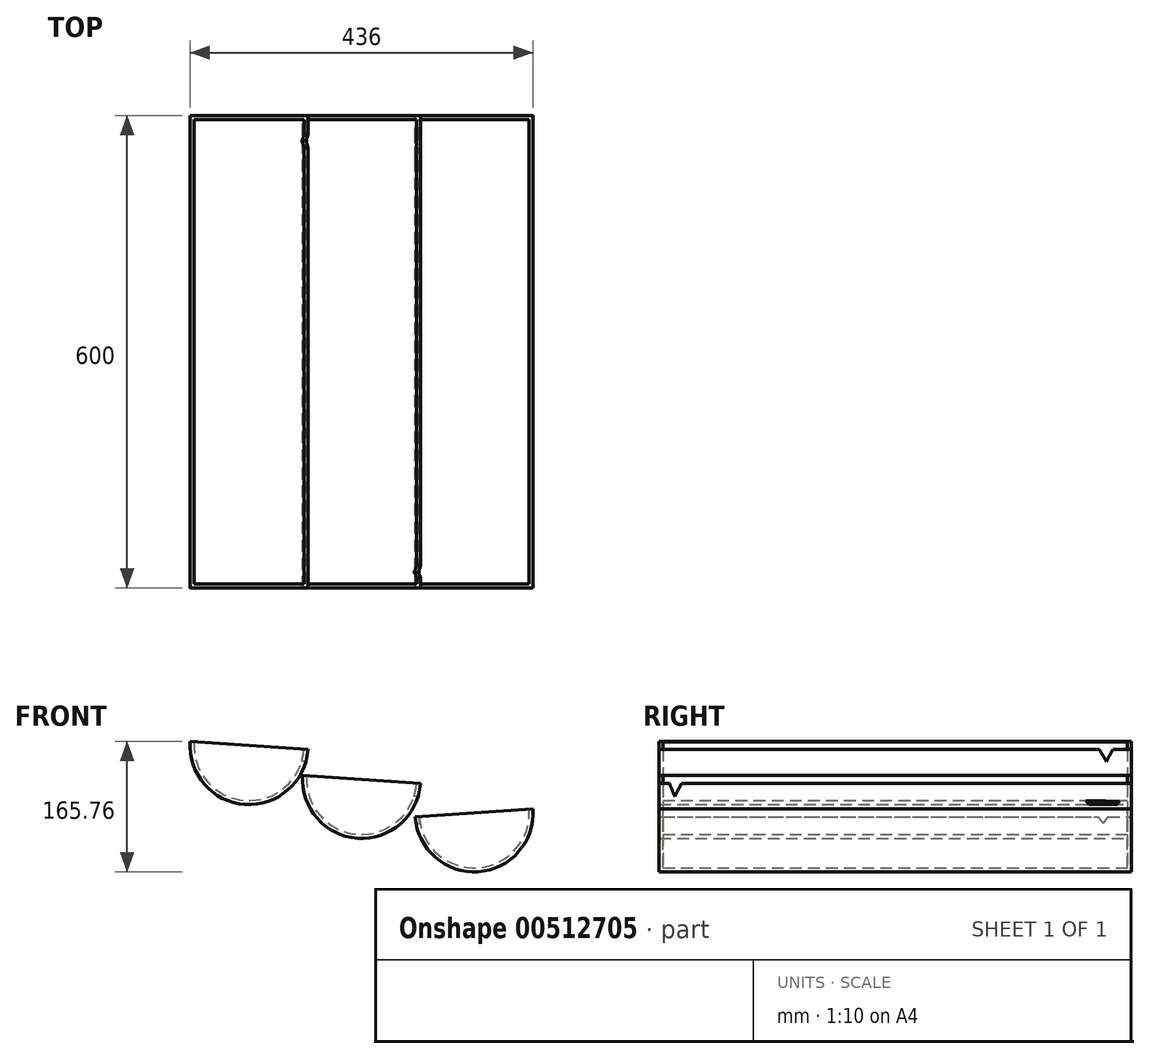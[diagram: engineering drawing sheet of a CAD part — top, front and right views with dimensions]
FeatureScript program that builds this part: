
annotation { "Feature Type Name" : "Feature", "Feature Type Description" : "" }
export const myFeature = defineFeature(function(context is Context, id is Id, definition is map)
    precondition{}
    {
        {
            var Q0;
            Q0=qCreatedBy(makeId("Front.planeOp"),FACE);
            var sketch = newSketch(context, id + "F0", { "sketchPlane" : qUnion([Q0])});
            skArc(sketch, "E0", {"start": v(75, 0) * mm, "mid": v(0, -75) * mm, "end": v(-75, 0) * mm});
            skArc(sketch, "E1", {"start": v(70, 0) * mm, "mid": v(0, -70) * mm, "end": v(-70, 0) * mm});
            skLineSegment(sketch, "E2", {"start": v(-75, 0) * mm, "end": v(-70, 0) * mm});
            skLineSegment(sketch, "E3", {"start": v(70, 0) * mm, "end": v(75, 0) * mm});
            skSolve(sketch);
        }
        {
            var Q0;
            Q0 = qSketchRegion(id + "F0", true);
            extrude(context, id + "F1", {"entities" : qUnion([Q0]), "depth" : 600 * mm});
        }
        {
            var Q0;
            Q0=makeQuery(id+"F1.opExtrude","CAP_FACE",FACE,{"disambiguationData":[OSD([sQuery(id+"F0.wireOp",EDGE,"E0"),sQuery(id+"F0.wireOp",EDGE,"E1"),sQuery(id+"F0.wireOp",EDGE,"E2"),sQuery(id+"F0.wireOp",EDGE,"E3")])],"isStart":false});
            var sketch = newSketch(context, id + "F2", { "sketchPlane" : qUnion([Q0])});
            skLineSegment(sketch, "E4", {"start": v(-70, 0) * mm, "end": v(70, 0) * mm});
            skArc(sketch, "E5.0", {"start": v(70, 0) * mm, "mid": v(0, -70) * mm, "end": v(-70, 0) * mm});
            skSolve(sketch);
        }
        {
            var Q0;
            Q0=makeQuery(id+"F2.imprint","IMPRINT",FACE,{"disambiguationData":[TD([[makeQuery(id+"F2.imprint","IMPRINT",EDGE,{"derivedFrom":sQuery(id+"F2.wireOp",EDGE,"E4")}),-1.0]])]});
            extrude(context, id + "F3", {"entities" : qUnion([Q0]), "operationType" : NewBodyOperationType.ADD, "oppositeDirection" : true, "depth" : 5 * mm});
        }
        {
            var Q0;
            Q0=makeQuery(id+"F1.opExtrude","CAP_FACE",FACE,{"disambiguationData":[OSD([sQuery(id+"F0.wireOp",EDGE,"E0"),sQuery(id+"F0.wireOp",EDGE,"E1"),sQuery(id+"F0.wireOp",EDGE,"E2"),sQuery(id+"F0.wireOp",EDGE,"E3")])],"isStart":true});
            var sketch = newSketch(context, id + "F4", { "sketchPlane" : qUnion([Q0])});
            skLineSegment(sketch, "E6", {"start": v(-70, 0) * mm, "end": v(70, 0) * mm});
            skArc(sketch, "E7.0", {"start": v(-70, 0) * mm, "mid": v(0, -70) * mm, "end": v(70, 0) * mm});
            skSolve(sketch);
        }
        {
            var Q0;
            Q0 = qSketchRegion(id + "F4", true);
            extrude(context, id + "F5", {"entities" : qUnion([Q0]), "operationType" : NewBodyOperationType.ADD, "oppositeDirection" : true, "depth" : 5 * mm});
        }
        {
            var Q0;
            Q0=makeQuery(id+"F1.opExtrude","SWEPT_BODY",BODY,{"disambiguationData":[OSD([sQuery(id+"F0.wireOp",EDGE,"E0"),sQuery(id+"F0.wireOp",EDGE,"E1"),sQuery(id+"F0.wireOp",EDGE,"E2"),sQuery(id+"F0.wireOp",EDGE,"E3")])]});
            var Q1;
            Q1=makeQuery(id+"F1.opExtrude","SWEPT_EDGE",EDGE,{"disambiguationData":[OSD([sQuery(id+"F0.wireOp",EDGE,"E0"),sQuery(id+"F0.wireOp",EDGE,"E3")])]});
            transform(context, id + "F6", {"entities" : qUnion([Q0]), "transformType" : TransformType.ROTATION, "transformAxis" : qUnion([Q1]), "angle" : 4 * degree, "makeCopy" : false});
        }
        {
            var Q0;
            Q0=makeQuery(id+"F1.opExtrude","SWEPT_BODY",BODY,{"disambiguationData":[OSD([sQuery(id+"F0.wireOp",EDGE,"E0"),sQuery(id+"F0.wireOp",EDGE,"E1"),sQuery(id+"F0.wireOp",EDGE,"E2"),sQuery(id+"F0.wireOp",EDGE,"E3")])]});
            transform(context, id + "F7", {"entities" : qUnion([Q0]), "transformType" : TransformType.TRANSLATION_3D, "dx" : 143 * mm, "dy" : 0 * mm, "dz" : -43 * mm, "makeCopy" : true});
        }
        {
            var Q0;
            Q0=makeQuery(id+"F7.opPattern","COPY",BODY,{"derivedFrom":makeQuery(id+"F1.opExtrude","SWEPT_BODY",BODY,{"disambiguationData":[OSD([sQuery(id+"F0.wireOp",EDGE,"E0"),sQuery(id+"F0.wireOp",EDGE,"E1"),sQuery(id+"F0.wireOp",EDGE,"E2"),sQuery(id+"F0.wireOp",EDGE,"E3")])]}),"instanceName":"1"});
            transform(context, id + "F8", {"entities" : qUnion([Q0]), "transformType" : TransformType.TRANSLATION_3D, "dx" : 143 * mm, "dy" : 0 * mm, "dz" : -53 * mm, "makeCopy" : true});
        }
        {
            var Q0;
            Q0=qCreatedBy(makeId("Right.planeOp"),FACE);
            var sketch = newSketch(context, id + "F9", { "sketchPlane" : qUnion([Q0])});
            skLineSegment(sketch, "E8", {"start": v(-18.64, 10.07) * mm, "end": v(-31.86, -15.15) * mm});
            skLineSegment(sketch, "E9", {"start": v(-31.86, -15.15) * mm, "end": v(-47.47, 11.88) * mm});
            skLineSegment(sketch, "E10", {"start": v(-47.47, 11.88) * mm, "end": v(-18.64, 10.07) * mm});
            skSolve(sketch);
        }
        {
            var Q0;
            Q0 = qSketchRegion(id + "F9", true);
            extrude(context, id + "F10", {"entities" : qUnion([Q0]), "operationType" : NewBodyOperationType.REMOVE, "depth" : 178 * mm});
        }
        {
            var Q0;
            Q0=qCreatedBy(makeId("Right.planeOp"),FACE);
            cPlane(context, id + "F11", {"entities" : qUnion([Q0]), "cplaneType" : CPlaneType.OFFSET, "offset" : 166 * mm, "width" : 150 * mm, "height" : 150 * mm});
        }
        {
            var Q0;
            Q0=qCreatedBy(id+"F11.planeOp",FACE);
            var sketch = newSketch(context, id + "F12", { "sketchPlane" : qUnion([Q0])});
            skLineSegment(sketch, "E11", {"start": v(-588.65, -38.58) * mm, "end": v(-580.2, -59.32) * mm});
            skLineSegment(sketch, "E12", {"start": v(-580.2, -59.32) * mm, "end": v(-569.42, -39.18) * mm});
            skLineSegment(sketch, "E13", {"start": v(-569.42, -39.18) * mm, "end": v(-588.65, -38.58) * mm});
            skSolve(sketch);
        }
        {
            var Q0;
            Q0 = qSketchRegion(id + "F12", true);
            extrude(context, id + "F13", {"entities" : qUnion([Q0]), "operationType" : NewBodyOperationType.REMOVE, "depth" : 121 * mm});
        }
        {
            var Q0;
            Q0=qCreatedBy(id+"F11.planeOp",FACE);
            cPlane(context, id + "F14", {"entities" : qUnion([Q0]), "cplaneType" : CPlaneType.OFFSET, "offset" : 150 * mm, "width" : 150 * mm, "height" : 150 * mm});
        }
        {
            var Q0;
            Q0=qCreatedBy(id+"F14.planeOp",FACE);
            var sketch = newSketch(context, id + "F15", { "sketchPlane" : qUnion([Q0])});
            skLineSegment(sketch, "E14", {"start": v(-15.5, -65.73) * mm, "end": v(-35.93, -93.5) * mm});
            skLineSegment(sketch, "E15", {"start": v(-35.93, -93.5) * mm, "end": v(-57.79, -64.96) * mm});
            skLineSegment(sketch, "E16", {"start": v(-57.79, -64.96) * mm, "end": v(-15.5, -65.73) * mm});
            skSolve(sketch);
        }
        {
            var Q0;
            Q0=makeQuery(id+"F8.opPattern","COPY",BODY,{"derivedFrom":makeQuery(id+"F7.opPattern","COPY",BODY,{"derivedFrom":makeQuery(id+"F1.opExtrude","SWEPT_BODY",BODY,{"disambiguationData":[OSD([sQuery(id+"F0.wireOp",EDGE,"E0"),sQuery(id+"F0.wireOp",EDGE,"E1"),sQuery(id+"F0.wireOp",EDGE,"E2"),sQuery(id+"F0.wireOp",EDGE,"E3")])]}),"instanceName":"1"}),"instanceName":"1"});
            var Q1;
            Q1=makeQuery(id+"F8.opPattern","COPY",EDGE,{"derivedFrom":makeQuery(id+"F7.opPattern","COPY",EDGE,{"derivedFrom":makeQuery(id+"F1.opExtrude","SWEPT_EDGE",EDGE,{"disambiguationData":[OSD([sQuery(id+"F0.wireOp",EDGE,"E0"),sQuery(id+"F0.wireOp",EDGE,"E2")])]}),"instanceName":"1"}),"instanceName":"1"});
            transform(context, id + "F16", {"entities" : qUnion([Q0]), "transformType" : TransformType.ROTATION, "transformAxis" : qUnion([Q1]), "angle" : 8 * degree, "oppositeDirection" : true, "makeCopy" : false});
        }
        {
            var Q0;
            Q0 = qSketchRegion(id + "F15", true);
            extrude(context, id + "F17", {"entities" : qUnion([Q0]), "operationType" : NewBodyOperationType.REMOVE, "oppositeDirection" : true, "depth" : 105 * mm});
        }
    });
